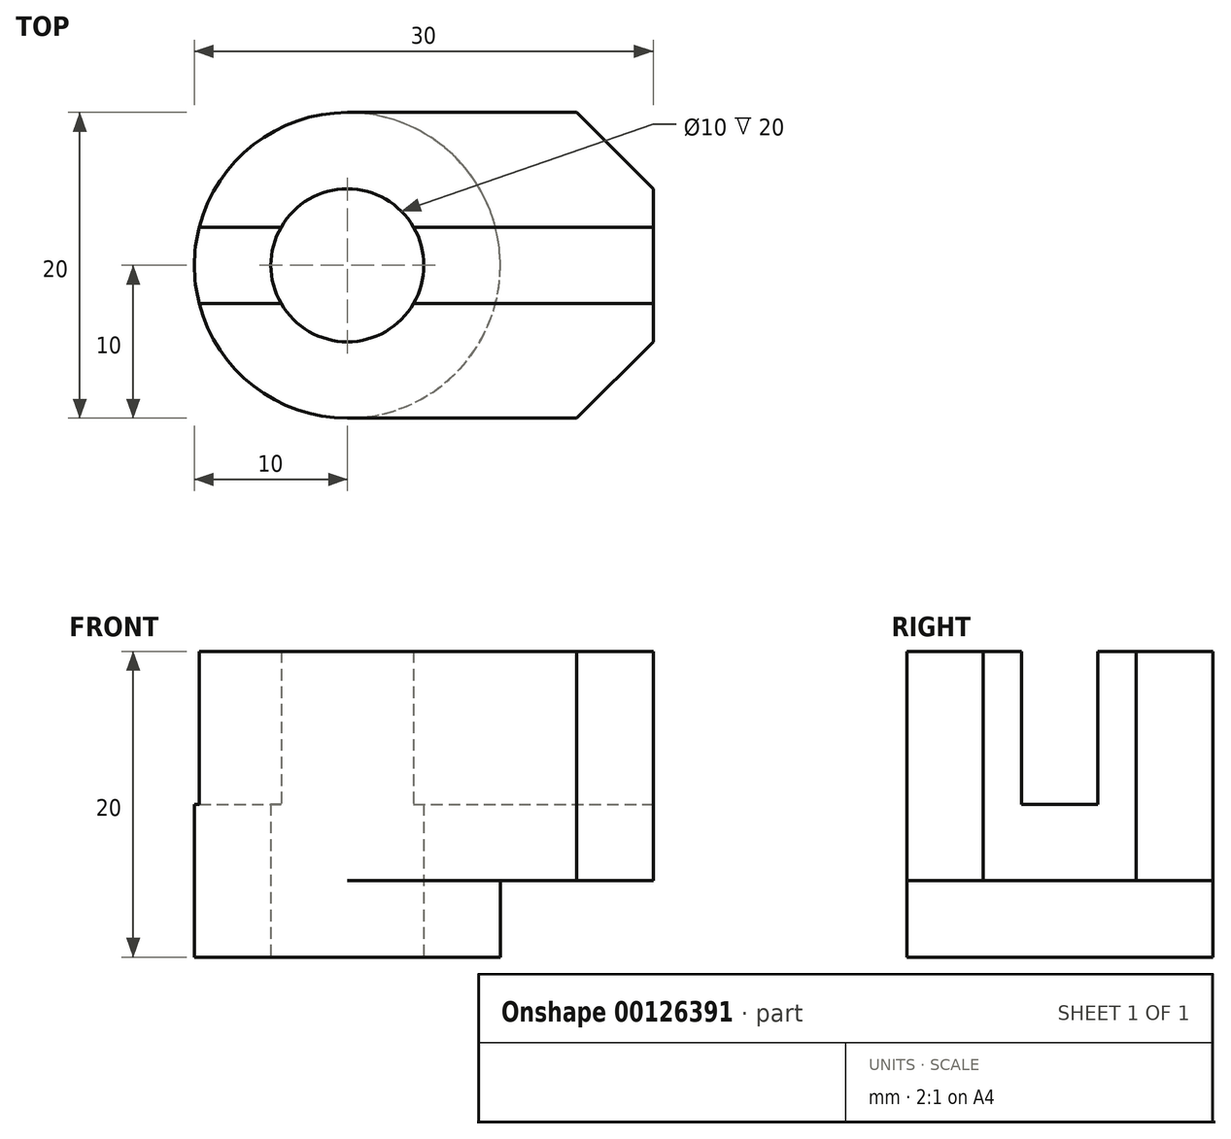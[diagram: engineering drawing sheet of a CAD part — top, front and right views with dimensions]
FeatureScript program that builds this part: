
annotation { "Feature Type Name" : "Feature", "Feature Type Description" : "" }
export const myFeature = defineFeature(function(context is Context, id is Id, definition is map)
    precondition{}
    {
        {
            var Q0;
            Q0=qCreatedBy(makeId("Top.planeOp"),FACE);
            var sketch = newSketch(context, id + "F0", { "sketchPlane" : qUnion([Q0])});
            skCircle(sketch, "E0", {"center": v(0, 0) * mm, "radius": 5 * mm});
            skCircle(sketch, "E1", {"center": v(0, 0) * mm, "radius": 10 * mm});
            skLineSegment(sketch, "E2", {"start": v(0, 10) * mm, "end": v(15, 10) * mm});
            skLineSegment(sketch, "E3", {"start": v(15, 10) * mm, "end": v(20, 5) * mm});
            skLineSegment(sketch, "E4", {"start": v(20, 5) * mm, "end": v(20, -5) * mm});
            skLineSegment(sketch, "E5", {"start": v(0, -10) * mm, "end": v(15, -10) * mm});
            skLineSegment(sketch, "E6", {"start": v(15, -10) * mm, "end": v(20, -5) * mm});
            skSolve(sketch);
        }
        {
            var Q0;
            Q0=makeQuery(id+"F0.imprint","IMPRINT",FACE,{"disambiguationData":[TD([[makeQuery(id+"F0.imprint","IMPRINT",EDGE,{"derivedFrom":sQuery(id+"F0.wireOp",EDGE,"E0")}),-1.0]])]});
            extrude(context, id + "F1", {"entities" : qUnion([Q0]), "depth" : 20 * mm});
        }
        {
            var Q0;
            {var subQ1=sQuery(id+"F0.wireOp",EDGE,"E2");Q0=makeQuery(id+"F0.imprint","IMPRINT",FACE,{"disambiguationData":[TD([[makeQuery(id+"F0.imprint","IMPRINT",EDGE,{"derivedFrom":subQ1}),-1.0]])]});}
            extrude(context, id + "F2", {"entities" : qUnion([Q0]), "operationType" : NewBodyOperationType.ADD, "depth" : 20 * mm});
        }
        {
            var Q0;
            Q0=makeQuery(id+"F2.opExtrude","SWEPT_FACE",FACE,{"disambiguationData":[OSD([sQuery(id+"F0.wireOp",EDGE,"E4")])]});
            var sketch = newSketch(context, id + "F3", { "sketchPlane" : qUnion([Q0])});
            skLineSegment(sketch, "E7.bottom", {"start": v(-2.5, 10) * mm, "end": v(2.5, 10) * mm});
            skLineSegment(sketch, "E7.top", {"start": v(-2.5, 20) * mm, "end": v(2.5, 20) * mm});
            skLineSegment(sketch, "E7.left", {"start": v(-2.5, 10) * mm, "end": v(-2.5, 20) * mm});
            skLineSegment(sketch, "E7.right", {"start": v(2.5, 10) * mm, "end": v(2.5, 20) * mm});
            skSolve(sketch);
        }
        {
            var Q0;
            Q0 = qSketchRegion(id + "F3", true);
            extrude(context, id + "F4", {"entities" : qUnion([Q0]), "operationType" : NewBodyOperationType.REMOVE, "oppositeDirection" : true, "depth" : 30 * mm});
        }
        {
            var Q0;
            {var subQ1=sQuery(id+"F0.wireOp",EDGE,"E2");Q0=makeQuery(id+"F0.imprint","IMPRINT",FACE,{"disambiguationData":[TD([[makeQuery(id+"F0.imprint","IMPRINT",EDGE,{"derivedFrom":subQ1}),-1.0]])]});}
            extrude(context, id + "F5", {"entities" : qUnion([Q0]), "operationType" : NewBodyOperationType.REMOVE, "depth" : 5 * mm});
        }
    });
